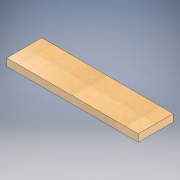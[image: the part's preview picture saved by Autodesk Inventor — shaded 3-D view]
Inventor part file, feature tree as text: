
AUTODESK INVENTOR PART (.ipt)
format: ipt  version: 2022.2 (Build 262287010, 287A)  size: 126,976 bytes
history: native  units: in
note: dims shown in document units (in); Inventor stores cm internally (conversion verified against a paired STEP export)
features: extrude x1, sketch x1
ambient origin geometry x8: Origin, YZ Plane, XZ Plane, XY Plane, X Axis, Y Axis, Z Axis, Center Point
bodies: Solid1 (feature_tree)
feature tree (2):
  extrude  "Extrusion1"  Depth=19.0in
  sketch  "Sketch1"  dims[d0=71.625in d1=19.0in d2=4.0in d3=0.0in]
